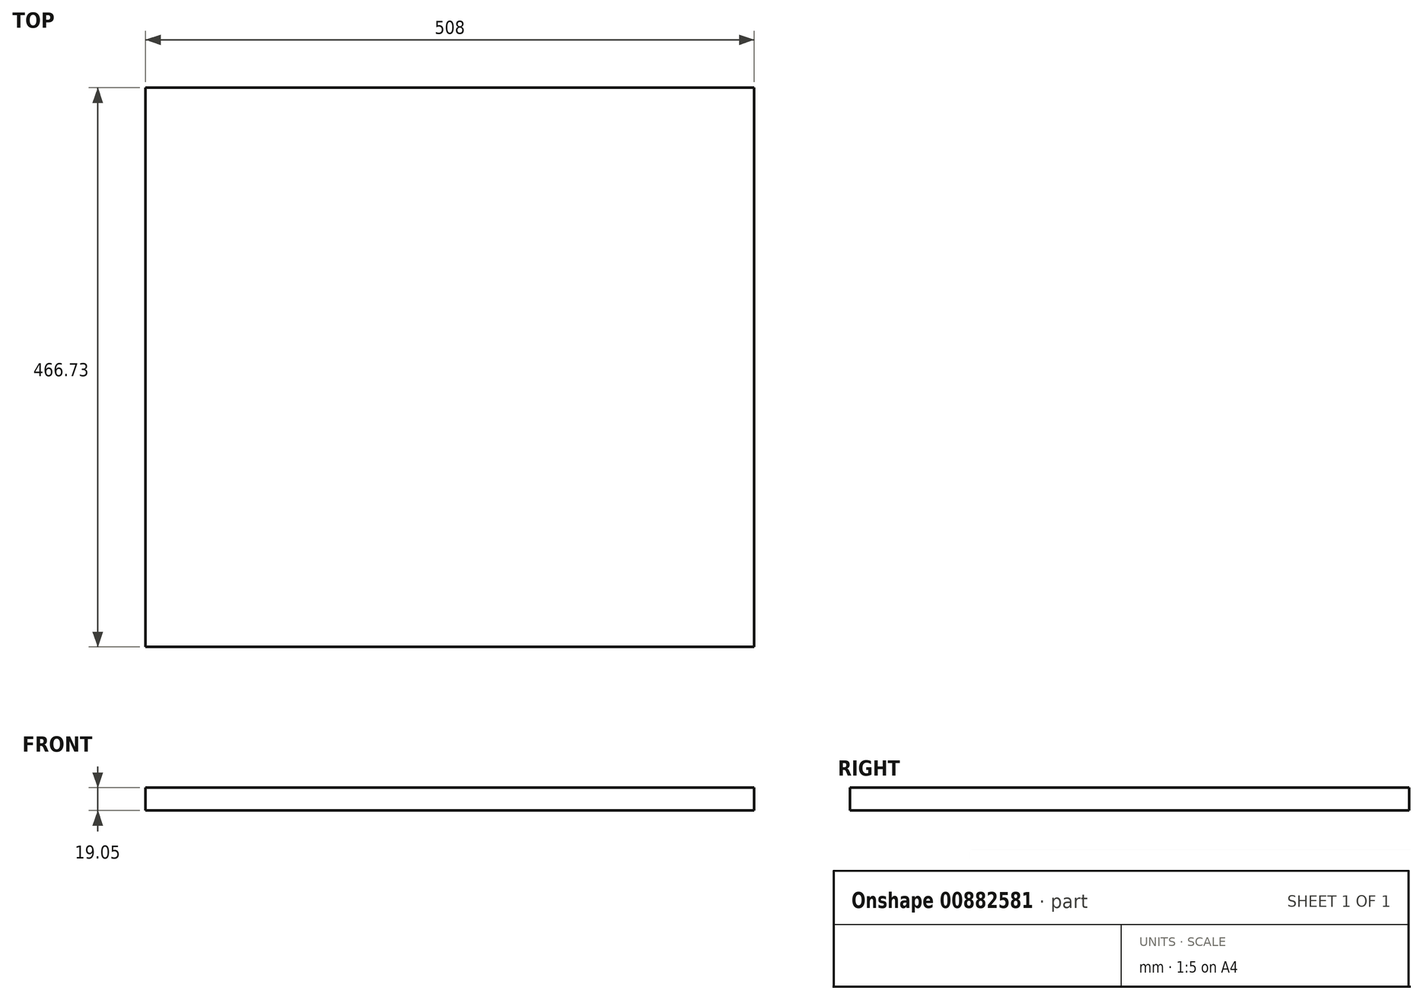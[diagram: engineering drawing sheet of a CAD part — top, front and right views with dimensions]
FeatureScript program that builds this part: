
annotation { "Feature Type Name" : "Feature", "Feature Type Description" : "" }
export const myFeature = defineFeature(function(context is Context, id is Id, definition is map)
    precondition{}
    {
        {
            var Q0;
            Q0=qCreatedBy(makeId("Top.planeOp"),FACE);
            var sketch = newSketch(context, id + "F0", { "sketchPlane" : qUnion([Q0])});
            skLineSegment(sketch, "E0.bottom", {"start": v(0, 0) * mm, "end": v(508, 0) * mm});
            skLineSegment(sketch, "E0.top", {"start": v(0, -466.73) * mm, "end": v(508, -466.73) * mm});
            skLineSegment(sketch, "E0.left", {"start": v(0, 0) * mm, "end": v(0, -466.73) * mm});
            skLineSegment(sketch, "E0.right", {"start": v(508, 0) * mm, "end": v(508, -466.73) * mm});
            skSolve(sketch);
        }
        {
            var Q0;
            Q0 = qSketchRegion(id + "F0", true);
            extrude(context, id + "F1", {"entities" : qUnion([Q0]), "depth" : 19.05 * mm, "offsetDistance" : 25.4 * mm});
        }
    });
